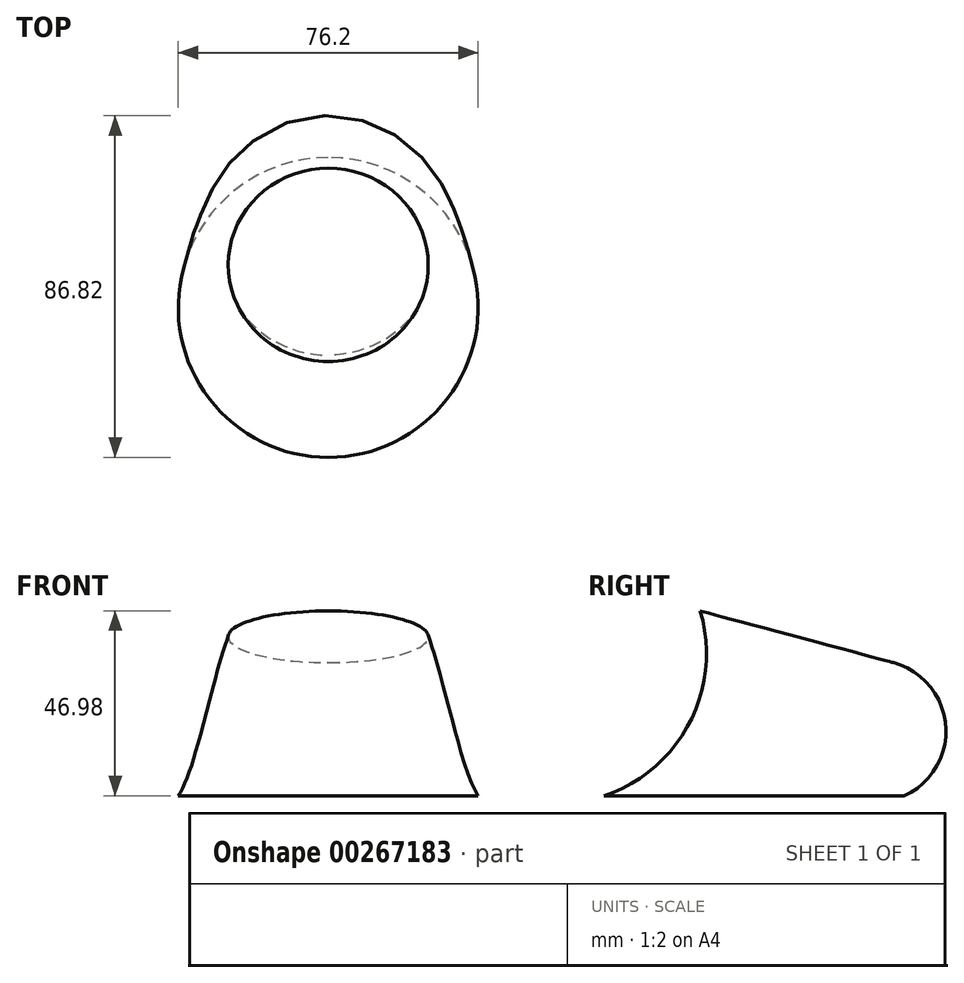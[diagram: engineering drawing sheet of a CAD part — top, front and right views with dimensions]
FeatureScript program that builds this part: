
annotation { "Feature Type Name" : "Feature", "Feature Type Description" : "" }
export const myFeature = defineFeature(function(context is Context, id is Id, definition is map)
    precondition{}
    {
        {
            var Q0;
            Q0=qCreatedBy(makeId("Top.planeOp"),FACE);
            var sketch = newSketch(context, id + "F0", { "sketchPlane" : qUnion([Q0])});
            skCircle(sketch, "E0", {"center": v(0, 0) * mm, "radius": 38.1 * mm});
            skLineSegment(sketch, "E1.top", {"start": v(63.5, 63.5) * mm, "end": v(-63.5, 63.5) * mm, "construction": true});
            skSolve(sketch);
        }
        {
            var Q0;
            Q0=sQuery(id+"F0.wireOp",EDGE,"E1.top");
            cPlane(context, id + "F1", {"entities" : qUnion([Q0]), "cplaneType" : CPlaneType.LINE_ANGLE, "offset" : 25.4 * mm, "angle" : 75 * degree, "oppositeDirection" : true, "width" : 152.4 * mm, "height" : 152.4 * mm});
        }
        {
            var Q0;
            Q0=qCreatedBy(id+"F1.planeOp",FACE);
            cPlane(context, id + "F2", {"entities" : qUnion([Q0]), "cplaneType" : CPlaneType.OFFSET, "offset" : 25.4 * mm, "oppositeDirection" : true, "width" : 152.4 * mm, "height" : 152.4 * mm});
        }
        {
            var Q0;
            Q0=qCreatedBy(id+"F2.planeOp",FACE);
            var sketch = newSketch(context, id + "F3", { "sketchPlane" : qUnion([Q0])});
            skCircle(sketch, "E2", {"center": v(0, 0) * mm, "radius": 25.4 * mm});
            skSolve(sketch);
        }
        {
            var Q0;
            Q0=qCreatedBy(makeId("Right.planeOp"),FACE);
            var sketch = newSketch(context, id + "F4", { "sketchPlane" : qUnion([Q0])});
            skLineSegment(sketch, "E3.0", {"start": v(35.36, 33.84) * mm, "end": v(-13.7, 46.98) * mm});
            skLineSegment(sketch, "E3.1", {"start": v(-38.1, 0) * mm, "end": v(38.1, 0) * mm});
            skArc(sketch, "E4", {"start": v(-38.1, 0) * mm, "mid": v(-16.41, 18.56) * mm, "end": v(-13.7, 46.98) * mm});
            skArc(sketch, "E5", {"start": v(35.36, 33.84) * mm, "mid": v(48.66, 17.88) * mm, "end": v(38.1, 0) * mm});
            skSolve(sketch);
        }
        {
            var Q0;
            Q0=makeQuery(id+"F0.imprint","IMPRINT",FACE,{"disambiguationData":[TD([[makeQuery(id+"F0.imprint","IMPRINT",EDGE,{"derivedFrom":sQuery(id+"F0.wireOp",EDGE,"E0")}),1.0]])]});
            var Q1;
            Q1=makeQuery(id+"F3.imprint","IMPRINT",FACE,{"disambiguationData":[TD([[makeQuery(id+"F3.imprint","IMPRINT",EDGE,{"derivedFrom":sQuery(id+"F3.wireOp",EDGE,"E2")}),1.0]])]});
            var Q2;
            Q2=sQuery(id+"F4.wireOp",EDGE,"E4");
            var Q3;
            Q3=sQuery(id+"F4.wireOp",EDGE,"E5");
            loft(context, id + "F5", {"addGuides" : true, "sheetProfilesArray" : [{ "sheetProfileEntities" : qUnion([Q0]) }, { "sheetProfileEntities" : qUnion([Q1]) }], "guidesArray" : [{ "guideEntities" : qUnion([Q2]), "guideDerivativeType" : LoftGuideDerivativeType.DEFAULT, "guideDerivativeMagnitude" : 1 }, { "guideEntities" : qUnion([Q3]), "guideDerivativeType" : LoftGuideDerivativeType.DEFAULT, "guideDerivativeMagnitude" : 1 }]});
        }
    });
